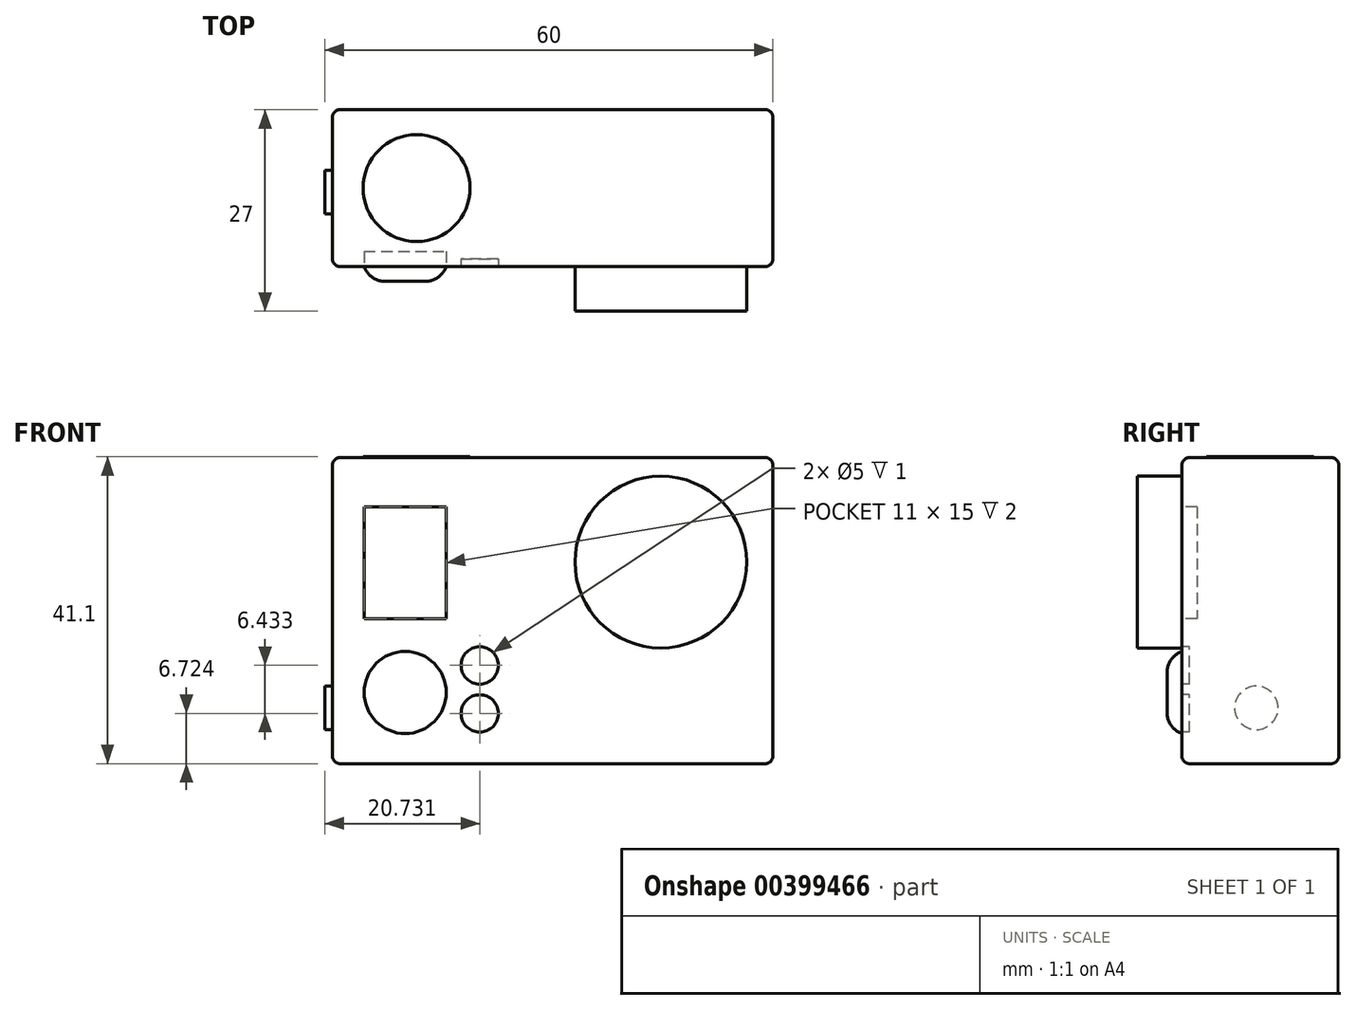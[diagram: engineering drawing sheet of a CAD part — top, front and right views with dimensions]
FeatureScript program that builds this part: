
annotation { "Feature Type Name" : "Feature", "Feature Type Description" : "" }
export const myFeature = defineFeature(function(context is Context, id is Id, definition is map)
    precondition{}
    {
        {
            var Q0;
            Q0=qCreatedBy(makeId("Front.planeOp"),FACE);
            var sketch = newSketch(context, id + "F0", { "sketchPlane" : qUnion([Q0])});
            skLineSegment(sketch, "E0.bottom", {"start": v(0, 0) * mm, "end": v(-59, 0) * mm});
            skLineSegment(sketch, "E0.top", {"start": v(0, 41) * mm, "end": v(-59, 41) * mm});
            skLineSegment(sketch, "E0.left", {"start": v(0, 0) * mm, "end": v(0, 41) * mm});
            skLineSegment(sketch, "E0.right", {"start": v(-59, 0) * mm, "end": v(-59, 41) * mm});
            skSolve(sketch);
        }
        {
            var Q0;
            Q0=makeQuery(id+"F0.imprint","IMPRINT",FACE,{"disambiguationData":[TD([[makeQuery(id+"F0.imprint","IMPRINT",EDGE,{"derivedFrom":sQuery(id+"F0.wireOp",EDGE,"E0.bottom")}),-1.0]])]});
            extrude(context, id + "F1", {"entities" : qUnion([Q0]), "depth" : 21 * mm});
        }
        {
            var Q0;
            Q0=makeQuery(id+"F1.opExtrude","CAP_FACE",FACE,{"disambiguationData":[OSD([sQuery(id+"F0.wireOp",EDGE,"E0.bottom"),sQuery(id+"F0.wireOp",EDGE,"E0.top"),sQuery(id+"F0.wireOp",EDGE,"E0.left"),sQuery(id+"F0.wireOp",EDGE,"E0.right")])],"isStart":false});
            var sketch = newSketch(context, id + "F2", { "sketchPlane" : qUnion([Q0])});
            skLineSegment(sketch, "E1", {"start": v(0, 41) * mm, "end": v(0, 27) * mm});
            skLineSegment(sketch, "E2", {"start": v(0, 27) * mm, "end": v(-15, 27) * mm});
            skCircle(sketch, "E3", {"center": v(-15, 27) * mm, "radius": 11.5 * mm});
            skLineSegment(sketch, "E4.bottom", {"start": v(-54.76, 34.38) * mm, "end": v(-43.76, 34.38) * mm});
            skLineSegment(sketch, "E4.top", {"start": v(-54.76, 19.38) * mm, "end": v(-43.76, 19.38) * mm});
            skLineSegment(sketch, "E4.left", {"start": v(-54.76, 34.38) * mm, "end": v(-54.76, 19.38) * mm});
            skLineSegment(sketch, "E4.right", {"start": v(-43.76, 34.38) * mm, "end": v(-43.76, 19.38) * mm});
            skLineSegment(sketch, "E5", {"start": v(-49.26, 19.38) * mm, "end": v(-49.26, 5.16) * mm, "construction": true});
            skCircle(sketch, "E6", {"center": v(-49.26, 9.53) * mm, "radius": 5.5 * mm});
            skCircle(sketch, "E7", {"center": v(-39.27, 13.16) * mm, "radius": 2.5 * mm});
            skCircle(sketch, "E8", {"center": v(-39.27, 6.72) * mm, "radius": 2.5 * mm});
            skSolve(sketch);
        }
        {
            var Q0;
            Q0=makeQuery(id+"F2.imprint","IMPRINT",FACE,{"disambiguationData":[TD([[makeQuery(id+"F2.imprint","IMPRINT",EDGE,{"derivedFrom":sQuery(id+"F2.wireOp",EDGE,"E3")}),1.0]])]});
            extrude(context, id + "F3", {"entities" : qUnion([Q0]), "operationType" : NewBodyOperationType.ADD, "depth" : 6 * mm});
        }
        {
            var Q0;
            Q0=makeQuery(id+"F2.imprint","IMPRINT",FACE,{"disambiguationData":[TD([[makeQuery(id+"F2.imprint","IMPRINT",EDGE,{"derivedFrom":sQuery(id+"F2.wireOp",EDGE,"E4.bottom")}),-1.0]])]});
            extrude(context, id + "F4", {"entities" : qUnion([Q0]), "operationType" : NewBodyOperationType.REMOVE, "oppositeDirection" : true, "depth" : 2 * mm});
        }
        {
            var Q0;
            Q0=makeQuery(id+"F2.imprint","IMPRINT",FACE,{"disambiguationData":[TD([[makeQuery(id+"F2.imprint","IMPRINT",EDGE,{"derivedFrom":sQuery(id+"F2.wireOp",EDGE,"E6")}),1.0]])]});
            var Q1;
            Q1=sQuery(id+"F2.wireOp",EDGE,"E6");
            extrude(context, id + "F5", {"entities" : qUnion([Q0]), "operationType" : NewBodyOperationType.ADD, "surfaceEntities" : qUnion([Q1]), "depth" : 2 * mm});
        }
        {
            var Q0;
            Q0=makeQuery(id+"F5.opExtrude","CAP_EDGE",EDGE,{"disambiguationData":[OSD([sQuery(id+"F2.wireOp",EDGE,"E6")])],"isStart":false});
            fillet(context, id + "F6", {"entities" : qUnion([Q0]), "radius" : 3 * mm, "tangentPropagation" : true, "allowEdgeOverflow" : false});
        }
        {
            var Q0;
            Q0=makeQuery(id+"F2.imprint","IMPRINT",FACE,{"disambiguationData":[TD([[makeQuery(id+"F2.imprint","IMPRINT",EDGE,{"derivedFrom":sQuery(id+"F2.wireOp",EDGE,"E7")}),1.0]])]});
            var Q1;
            Q1=makeQuery(id+"F2.imprint","IMPRINT",FACE,{"disambiguationData":[TD([[makeQuery(id+"F2.imprint","IMPRINT",EDGE,{"derivedFrom":sQuery(id+"F2.wireOp",EDGE,"E8")}),1.0]])]});
            extrude(context, id + "F7", {"entities" : qUnion([Q0, Q1]), "operationType" : NewBodyOperationType.REMOVE, "oppositeDirection" : true, "depth" : 1 * mm});
        }
        {
            var Q0;
            Q0=makeQuery(id+"F1.opExtrude","SWEPT_FACE",FACE,{"disambiguationData":[OSD([sQuery(id+"F0.wireOp",EDGE,"E0.right")])]});
            var sketch = newSketch(context, id + "F8", { "sketchPlane" : qUnion([Q0])});
            skCircle(sketch, "E9", {"center": v(11.04, 7.47) * mm, "radius": 2.91 * mm});
            skSolve(sketch);
        }
        {
            var Q0;
            Q0=makeQuery(id+"F8.imprint","IMPRINT",FACE,{"disambiguationData":[TD([[makeQuery(id+"F8.imprint","IMPRINT",EDGE,{"derivedFrom":sQuery(id+"F8.wireOp",EDGE,"E9")}),1.0]])]});
            extrude(context, id + "F9", {"entities" : qUnion([Q0]), "operationType" : NewBodyOperationType.ADD, "depth" : 1 * mm});
        }
        {
            var Q0;
            Q0=makeQuery(id+"F1.opExtrude","SWEPT_FACE",FACE,{"disambiguationData":[OSD([sQuery(id+"F0.wireOp",EDGE,"E0.top")])]});
            var sketch = newSketch(context, id + "F10", { "sketchPlane" : qUnion([Q0])});
            skCircle(sketch, "E10", {"center": v(-47.73, -10.5) * mm, "radius": 7.17 * mm});
            skPoint(sketch, "E10.centerSnap0", {"position": v(-59, -10.5) * mm});
            skSolve(sketch);
        }
        {
            var Q0;
            Q0=makeQuery(id+"F10.imprint","IMPRINT",FACE,{"disambiguationData":[TD([[makeQuery(id+"F10.imprint","IMPRINT",EDGE,{"derivedFrom":sQuery(id+"F10.wireOp",EDGE,"E10")}),1.0]])]});
            extrude(context, id + "F11", {"entities" : qUnion([Q0]), "operationType" : NewBodyOperationType.ADD, "depth" : .1 * mm});
        }
        {
            var Q0;
            Q0=makeQuery(id+"F1.opExtrude","CAP_EDGE",EDGE,{"disambiguationData":[OSD([sQuery(id+"F0.wireOp",EDGE,"E0.top")])],"isStart":false});
            var Q1;
            Q1=makeQuery(id+"F1.opExtrude","SWEPT_EDGE",EDGE,{"disambiguationData":[OSD([sQuery(id+"F0.wireOp",EDGE,"E0.top"),sQuery(id+"F0.wireOp",EDGE,"E0.right")])]});
            var Q2;
            Q2=makeQuery(id+"F1.opExtrude","CAP_EDGE",EDGE,{"disambiguationData":[OSD([sQuery(id+"F0.wireOp",EDGE,"E0.top")])],"isStart":true});
            var Q3;
            Q3=makeQuery(id+"F1.opExtrude","SWEPT_EDGE",EDGE,{"disambiguationData":[OSD([sQuery(id+"F0.wireOp",EDGE,"E0.top"),sQuery(id+"F0.wireOp",EDGE,"E0.left")])]});
            var Q4;
            Q4=makeQuery(id+"F1.opExtrude","CAP_EDGE",EDGE,{"disambiguationData":[OSD([sQuery(id+"F0.wireOp",EDGE,"E0.right")])],"isStart":false});
            var Q5;
            Q5=makeQuery(id+"F1.opExtrude","CAP_EDGE",EDGE,{"disambiguationData":[OSD([sQuery(id+"F0.wireOp",EDGE,"E0.right")])],"isStart":true});
            var Q6;
            Q6=makeQuery(id+"F1.opExtrude","CAP_EDGE",EDGE,{"disambiguationData":[OSD([sQuery(id+"F0.wireOp",EDGE,"E0.left")])],"isStart":false});
            var Q7;
            Q7=makeQuery(id+"F1.opExtrude","CAP_EDGE",EDGE,{"disambiguationData":[OSD([sQuery(id+"F0.wireOp",EDGE,"E0.left")])],"isStart":true});
            var Q8;
            Q8=makeQuery(id+"F1.opExtrude","SWEPT_EDGE",EDGE,{"disambiguationData":[OSD([sQuery(id+"F0.wireOp",EDGE,"E0.bottom"),sQuery(id+"F0.wireOp",EDGE,"E0.left")])]});
            var Q9;
            Q9=makeQuery(id+"F1.opExtrude","CAP_EDGE",EDGE,{"disambiguationData":[OSD([sQuery(id+"F0.wireOp",EDGE,"E0.bottom")])],"isStart":false});
            var Q10;
            Q10=makeQuery(id+"F1.opExtrude","CAP_EDGE",EDGE,{"disambiguationData":[OSD([sQuery(id+"F0.wireOp",EDGE,"E0.bottom")])],"isStart":true});
            var Q11;
            Q11=makeQuery(id+"F1.opExtrude","SWEPT_EDGE",EDGE,{"disambiguationData":[OSD([sQuery(id+"F0.wireOp",EDGE,"E0.bottom"),sQuery(id+"F0.wireOp",EDGE,"E0.right")])]});
            fillet(context, id + "F12", {"entities" : qUnion([Q0, Q1, Q2, Q3, Q4, Q5, Q6, Q7, Q8, Q9, Q10, Q11]), "radius" : 1 * mm, "tangentPropagation" : true, "allowEdgeOverflow" : false});
        }
    });
